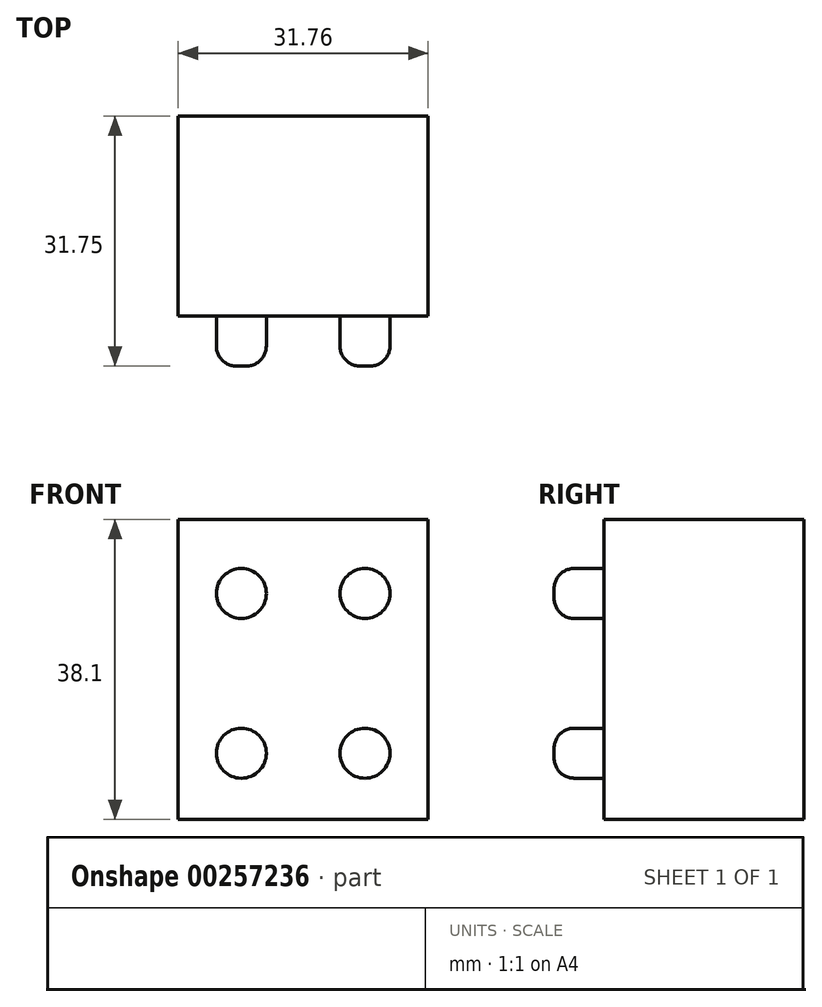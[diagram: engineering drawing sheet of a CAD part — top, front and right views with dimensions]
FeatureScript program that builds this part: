
annotation { "Feature Type Name" : "Feature", "Feature Type Description" : "" }
export const myFeature = defineFeature(function(context is Context, id is Id, definition is map)
    precondition{}
    {
        {
            var Q0;
            Q0=qCreatedBy(makeId("Front.planeOp"),FACE);
            var sketch = newSketch(context, id + "F0", { "sketchPlane" : qUnion([Q0])});
            skLineSegment(sketch, "E0.bottom", {"start": v(-15.87, 19.05) * mm, "end": v(15.88, 19.05) * mm});
            skLineSegment(sketch, "E0.top", {"start": v(-15.88, -19.05) * mm, "end": v(15.87, -19.05) * mm});
            skLineSegment(sketch, "E0.left", {"start": v(-15.87, 19.05) * mm, "end": v(-15.88, -19.05) * mm});
            skLineSegment(sketch, "E0.right", {"start": v(15.88, 19.05) * mm, "end": v(15.87, -19.05) * mm});
            skPoint(sketch, "E0.middle", {"position": v(0, 0) * mm});
            skSolve(sketch);
        }
        {
            var Q0;
            Q0 = qSketchRegion(id + "F0", true);
            extrude(context, id + "F1", {"entities" : qUnion([Q0]), "depth" : 25.4 * mm});
        }
        {
            var Q0;
            Q0=makeQuery(id+"F1.opExtrude","CAP_FACE",FACE,{"disambiguationData":[OSD([sQuery(id+"F0.wireOp",EDGE,"E0.bottom"),sQuery(id+"F0.wireOp",EDGE,"E0.top"),sQuery(id+"F0.wireOp",EDGE,"E0.left"),sQuery(id+"F0.wireOp",EDGE,"E0.right")])],"isStart":false});
            var sketch = newSketch(context, id + "F2", { "sketchPlane" : qUnion([Q0])});
            skCircle(sketch, "E1", {"center": v(-7.85, 9.65) * mm, "radius": 3.18 * mm});
            skCircle(sketch, "E2", {"center": v(7.85, 9.65) * mm, "radius": 3.18 * mm});
            skCircle(sketch, "E3", {"center": v(7.85, -10.64) * mm, "radius": 3.18 * mm});
            skCircle(sketch, "E4", {"center": v(-7.85, -10.64) * mm, "radius": 3.18 * mm});
            skSolve(sketch);
        }
        {
            var Q0;
            Q0=makeQuery(id+"F2.imprint","IMPRINT",FACE,{"disambiguationData":[TD([[makeQuery(id+"F2.imprint","IMPRINT",EDGE,{"derivedFrom":sQuery(id+"F2.wireOp",EDGE,"E1")}),1.0]])]});
            var Q1;
            Q1=makeQuery(id+"F2.imprint","IMPRINT",FACE,{"disambiguationData":[TD([[makeQuery(id+"F2.imprint","IMPRINT",EDGE,{"derivedFrom":sQuery(id+"F2.wireOp",EDGE,"E2")}),1.0]])]});
            var Q2;
            Q2=makeQuery(id+"F2.imprint","IMPRINT",FACE,{"disambiguationData":[TD([[makeQuery(id+"F2.imprint","IMPRINT",EDGE,{"derivedFrom":sQuery(id+"F2.wireOp",EDGE,"E4")}),1.0]])]});
            var Q3;
            Q3=makeQuery(id+"F2.imprint","IMPRINT",FACE,{"disambiguationData":[TD([[makeQuery(id+"F2.imprint","IMPRINT",EDGE,{"derivedFrom":sQuery(id+"F2.wireOp",EDGE,"E3")}),1.0]])]});
            extrude(context, id + "F3", {"entities" : qUnion([Q0, Q1, Q2, Q3]), "depth" : 6.35 * mm});
        }
        {
            var Q0;
            Q0=makeQuery(id+"F3.opExtrude","CAP_EDGE",EDGE,{"disambiguationData":[OSD([sQuery(id+"F2.wireOp",EDGE,"E1")])],"isStart":false});
            var Q1;
            Q1=makeQuery(id+"F3.opExtrude","CAP_EDGE",EDGE,{"disambiguationData":[OSD([sQuery(id+"F2.wireOp",EDGE,"E2")])],"isStart":false});
            var Q2;
            Q2=makeQuery(id+"F3.opExtrude","CAP_EDGE",EDGE,{"disambiguationData":[OSD([sQuery(id+"F2.wireOp",EDGE,"E3")])],"isStart":false});
            var Q3;
            Q3=makeQuery(id+"F3.opExtrude","CAP_EDGE",EDGE,{"disambiguationData":[OSD([sQuery(id+"F2.wireOp",EDGE,"E4")])],"isStart":false});
            fillet(context, id + "F4", {"entities" : qUnion([Q0, Q1, Q2, Q3]), "radius" : 2.54 * mm, "tangentPropagation" : true, "allowEdgeOverflow" : false});
        }
    });
